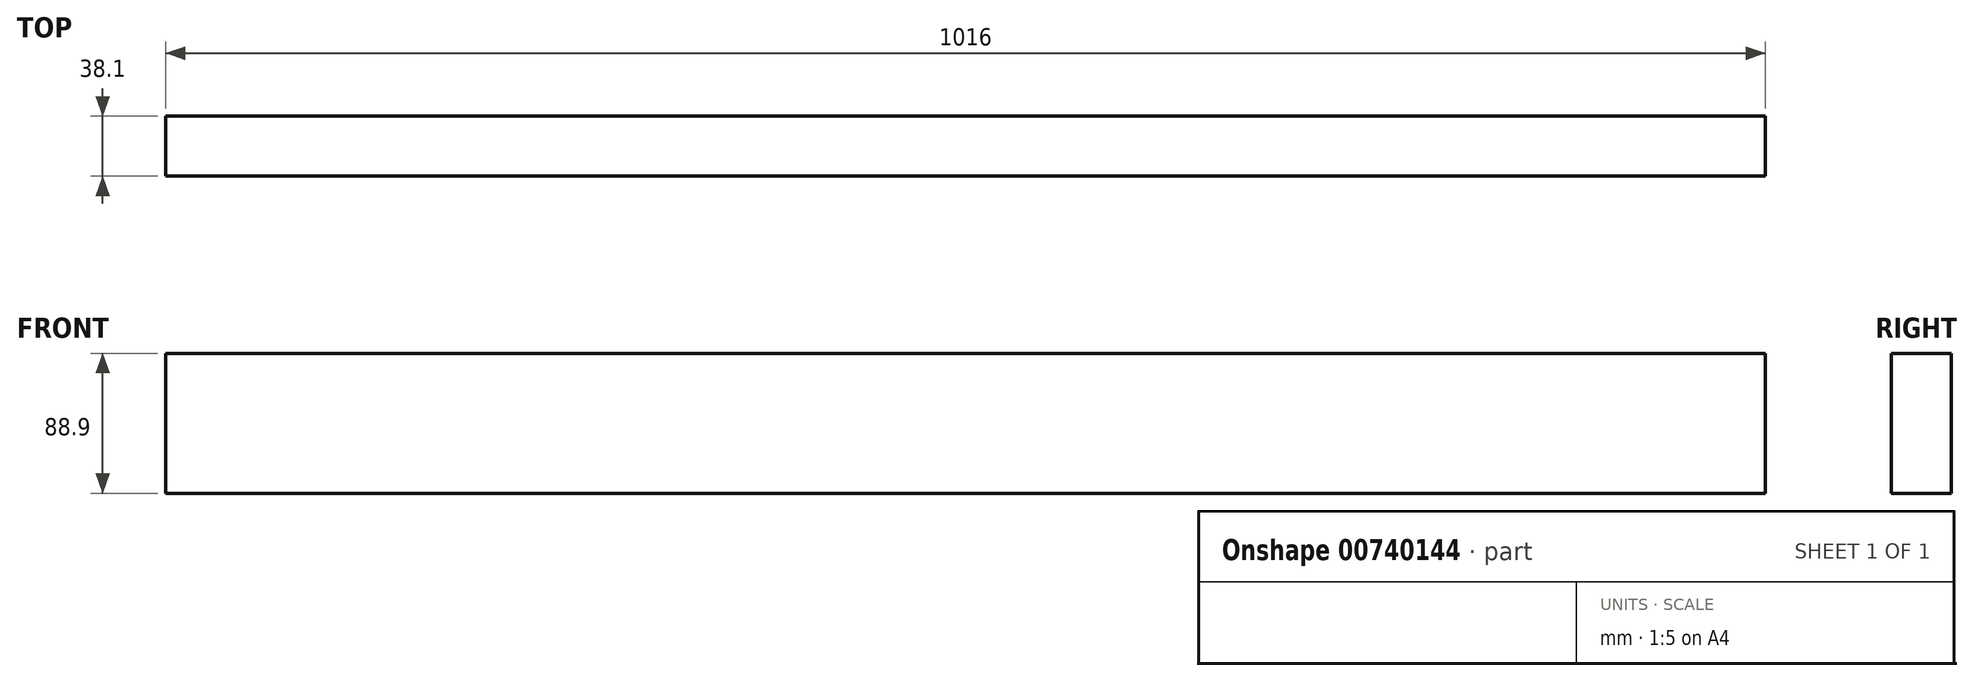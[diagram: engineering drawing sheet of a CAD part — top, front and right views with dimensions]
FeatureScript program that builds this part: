
annotation { "Feature Type Name" : "Feature", "Feature Type Description" : "" }
export const myFeature = defineFeature(function(context is Context, id is Id, definition is map)
    precondition{}
    {
        {
            var Q0;
            Q0=qCreatedBy(makeId("Right.planeOp"),FACE);
            var sketch = newSketch(context, id + "F0", { "sketchPlane" : qUnion([Q0])});
            skLineSegment(sketch, "E0.bottom", {"start": v(-79.68, 85.36) * mm, "end": v(-41.58, 85.36) * mm});
            skLineSegment(sketch, "E0.top", {"start": v(-79.68, -3.54) * mm, "end": v(-41.58, -3.54) * mm});
            skLineSegment(sketch, "E0.left", {"start": v(-79.68, 85.36) * mm, "end": v(-79.68, -3.54) * mm});
            skLineSegment(sketch, "E0.right", {"start": v(-41.58, 85.36) * mm, "end": v(-41.58, -3.54) * mm});
            skSolve(sketch);
        }
        {
            var Q0;
            Q0=makeQuery(id+"F0.imprint","IMPRINT",FACE,{"disambiguationData":[TD([[makeQuery(id+"F0.imprint","IMPRINT",EDGE,{"derivedFrom":sQuery(id+"F0.wireOp",EDGE,"E0.bottom")}),-1.0]])]});
            extrude(context, id + "F1", {"entities" : qUnion([Q0]), "depth" : 1016 * mm, "offsetDistance" : 25.4 * mm});
        }
    });
